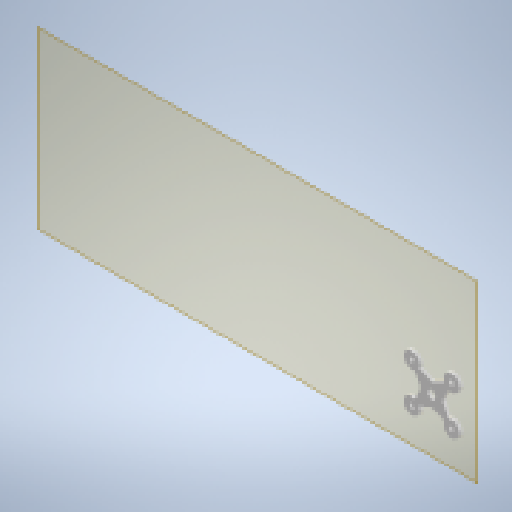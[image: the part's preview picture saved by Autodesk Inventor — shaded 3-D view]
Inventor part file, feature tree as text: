
AUTODESK INVENTOR PART (.ipt)
format: ipt  version: 2024.2 (Build 282272000, 272)  size: 163,840 bytes
history: native  units: mm
features: other x6, reference x5, extrude x1, sketch x1
ambient origin geometry x8: Origin, YZ Plane, XZ Plane, XY Plane, X Axis, Y Axis, Z Axis, Center Point
bodies: Body1 (feature_tree)
feature tree (13):
  other  "Твердое тело1"
  other  "РабПлоскость1"
  extrude  "Выдавливание1"  Depth=2.0mm
  sketch  "Эскиз1"
  reference  "Ссылка1"
  reference  "Ссылка2"
  reference  "Ссылка3"
  reference  "Ссылка4"
  reference  "Ссылка5"
  other  "<userpath>\Documents\Artist-v2\3D\Робот.iam"
  other  "Робот.iam"
  other  "бок:1"
  other  "бок:2"
